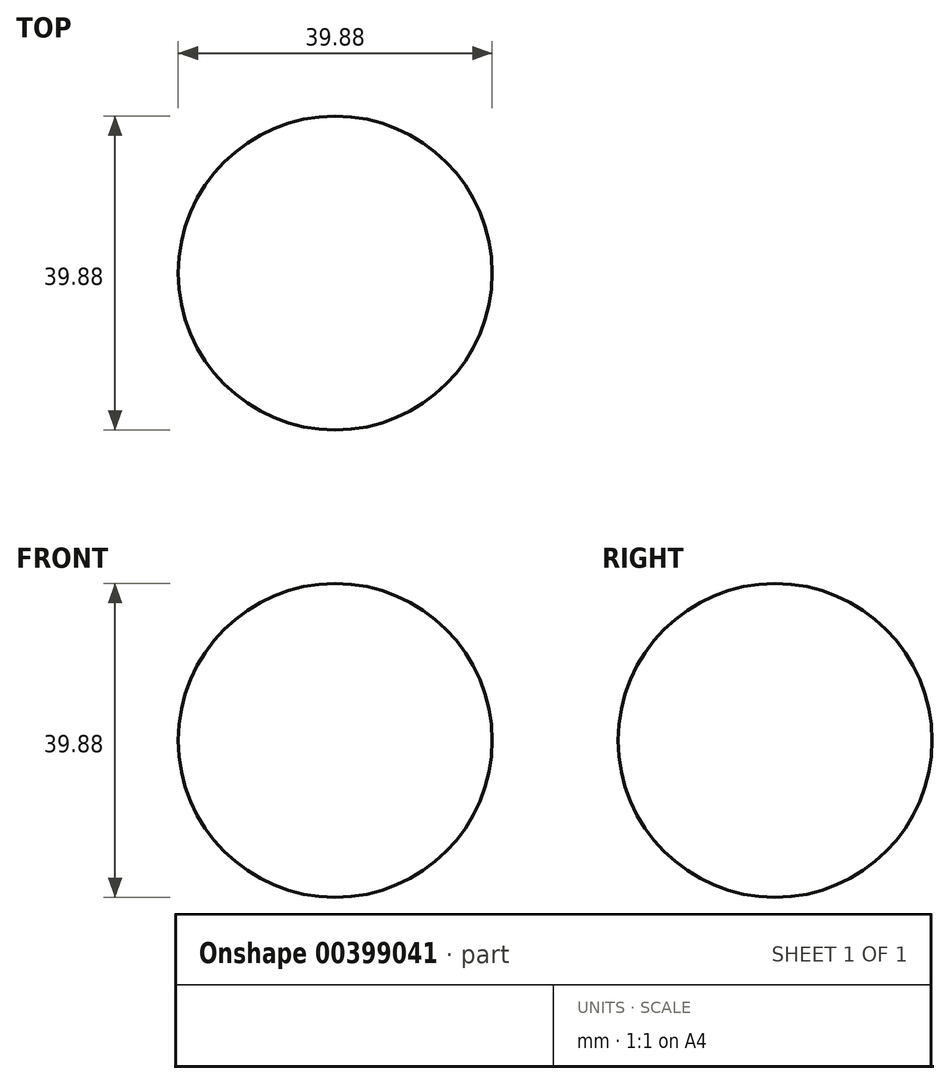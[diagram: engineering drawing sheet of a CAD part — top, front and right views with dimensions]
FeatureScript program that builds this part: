
annotation { "Feature Type Name" : "Feature", "Feature Type Description" : "" }
export const myFeature = defineFeature(function(context is Context, id is Id, definition is map)
    precondition{}
    {
        {
            var Q0;
            Q0=qCreatedBy(makeId("Top.planeOp"),FACE);
            var sketch = newSketch(context, id + "F0", { "sketchPlane" : qUnion([Q0])});
            skCircle(sketch, "E0", {"center": v(0, 0) * mm, "radius": 19.94 * mm});
            skLineSegment(sketch, "E1", {"start": v(0, 19.94) * mm, "end": v(0, -19.94) * mm});
            skSolve(sketch);
        }
        {
            var Q0;
            {var subQ0=sQuery(id+"F0.wireOp",EDGE,"E1");Q0=makeQuery(id+"F0.imprint","IMPRINT",FACE,{"disambiguationData":[TD([[makeQuery(id+"F0.imprint","IMPRINT",EDGE,{"derivedFrom":subQ0}),1.0]])]});}
            var Q1;
            Q1=sQuery(id+"F0.wireOp",EDGE,"E1");
            revolve(context, id + "F1", {"entities" : qUnion([Q0]), "axis" : qUnion([Q1]), "revolveType" : RevolveType.FULL});
        }
    });
